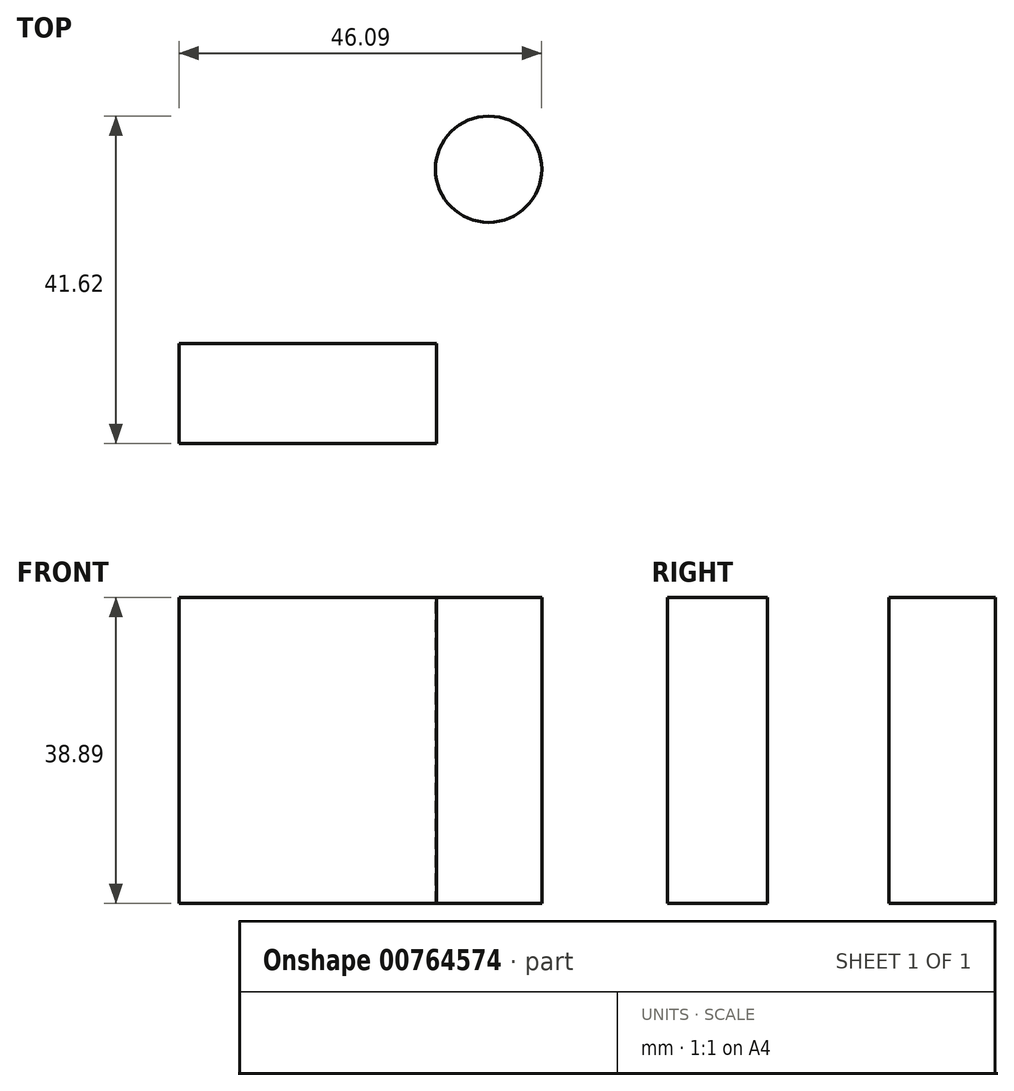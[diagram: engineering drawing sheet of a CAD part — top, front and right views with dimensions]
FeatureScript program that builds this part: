
annotation { "Feature Type Name" : "Feature", "Feature Type Description" : "" }
export const myFeature = defineFeature(function(context is Context, id is Id, definition is map)
    precondition{}
    {
        {
            var Q0;
            Q0=qCreatedBy(makeId("Front.planeOp"),FACE);
            var sketch = newSketch(context, id + "F0", { "sketchPlane" : qUnion([Q0])});
            skLineSegment(sketch, "E0.bottom", {"start": v(-66.48, 31.58) * mm, "end": v(-33.74, 31.58) * mm});
            skLineSegment(sketch, "E0.top", {"start": v(-66.48, -7.3) * mm, "end": v(-33.74, -7.3) * mm});
            skLineSegment(sketch, "E0.left", {"start": v(-66.48, 31.58) * mm, "end": v(-66.48, -7.3) * mm});
            skLineSegment(sketch, "E0.right", {"start": v(-33.74, 31.58) * mm, "end": v(-33.74, -7.3) * mm});
            skSolve(sketch);
        }
        {
            var Q0;
            Q0 = qSketchRegion(id + "F0", true);
            extrude(context, id + "F1", {"entities" : qUnion([Q0]), "depth" : 12.7 * mm, "offsetDistance" : 30.48 * mm});
        }
        {
            var Q0;
            Q0=qCreatedBy(makeId("Top.planeOp"),FACE);
            var sketch = newSketch(context, id + "F2", { "sketchPlane" : qUnion([Q0])});
            skCircle(sketch, "E1", {"center": v(-27.14, 22.17) * mm, "radius": 6.75 * mm});
            skSolve(sketch);
        }
        {
            var Q0;
            Q0=makeQuery(id+"F2.imprint","IMPRINT",FACE,{"disambiguationData":[TD([[makeQuery(id+"F2.imprint","IMPRINT",EDGE,{"derivedFrom":sQuery(id+"F2.wireOp",EDGE,"E1")}),1.0]])]});
            var Q1;
            Q1=makeQuery(id+"F1.opExtrude","CAP_EDGE",EDGE,{"disambiguationData":[OSD([sQuery(id+"F0.wireOp",EDGE,"E0.right")])],"isStart":true});
            sweep(context, id + "F3", {"profiles" : qUnion([Q0]), "path" : qUnion([Q1])});
        }
    });
